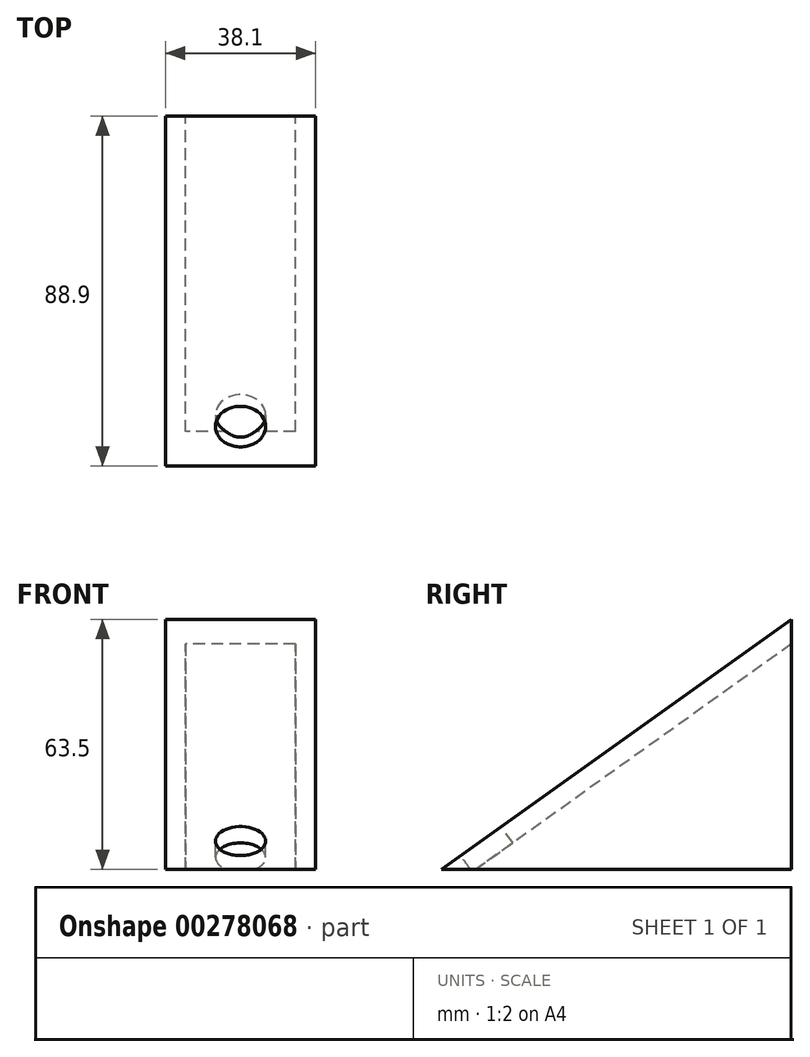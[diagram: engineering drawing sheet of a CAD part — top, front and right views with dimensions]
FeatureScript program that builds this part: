
annotation { "Feature Type Name" : "Feature", "Feature Type Description" : "" }
export const myFeature = defineFeature(function(context is Context, id is Id, definition is map)
    precondition{}
    {
        {
            var Q0;
            Q0=qCreatedBy(makeId("Right.planeOp"),FACE);
            var sketch = newSketch(context, id + "F0", { "sketchPlane" : qUnion([Q0])});
            skLineSegment(sketch, "E0", {"start": v(-34.77, -24.9) * mm, "end": v(54.13, -24.94) * mm});
            skLineSegment(sketch, "E1", {"start": v(54.13, -24.94) * mm, "end": v(54.13, 38.56) * mm});
            skLineSegment(sketch, "E2", {"start": v(54.13, 38.56) * mm, "end": v(-34.77, -24.9) * mm});
            skSolve(sketch);
        }
        {
            var Q0;
            Q0 = qSketchRegion(id + "F0", true);
            extrude(context, id + "F1", {"entities" : qUnion([Q0]), "depth" : 38.1 * mm});
        }
        {
            var Q0;
            Q0=makeQuery(id+"F1.opExtrude","SWEPT_FACE",FACE,{"disambiguationData":[OSD([sQuery(id+"F0.wireOp",EDGE,"E0")])]});
            var Q1;
            Q1=makeQuery(id+"F1.opExtrude","SWEPT_FACE",FACE,{"disambiguationData":[OSD([sQuery(id+"F0.wireOp",EDGE,"E1")])]});
            shell(context, id + "F2", {"entities" : qUnion([Q0, Q1]), "thickness" : 5.08 * mm});
        }
        {
            var Q0;
            Q0=makeQuery(id+"F1.opExtrude","SWEPT_FACE",FACE,{"disambiguationData":[OSD([sQuery(id+"F0.wireOp",EDGE,"E2")])]});
            var sketch = newSketch(context, id + "F3", { "sketchPlane" : qUnion([Q0])});
            skCircle(sketch, "E3", {"center": v(19.05, -30.45) * mm, "radius": 6.35 * mm});
            skPoint(sketch, "E3.centerSnap0", {"position": v(19.05, -42.76) * mm});
            skSolve(sketch);
        }
        {
            var Q0;
            Q0=sQuery(id+"F3.wireOp",VERTEX,"E3.center");
            var Q1;
            Q1=makeQuery(id+"F1.opExtrude","SWEPT_BODY",BODY,{"disambiguationData":[OSD([sQuery(id+"F0.wireOp",EDGE,"E0"),sQuery(id+"F0.wireOp",EDGE,"E1"),sQuery(id+"F0.wireOp",EDGE,"E2")])]});
            hole(context, id + "F4", {"style" : HoleStyle.C_BORE, "endStyle" : HoleEndStyle.THROUGH, "holeDiameter" : 6.35 * mm, "cBoreDiameter" : 12.7 * mm, "cBoreDepth" : 5.08 * mm, "tappedDepth" : 12.7 * mm, "tapClearance" : 3, "locations" : qUnion([Q0]), "scope" : qUnion([Q1])});
        }
    });
